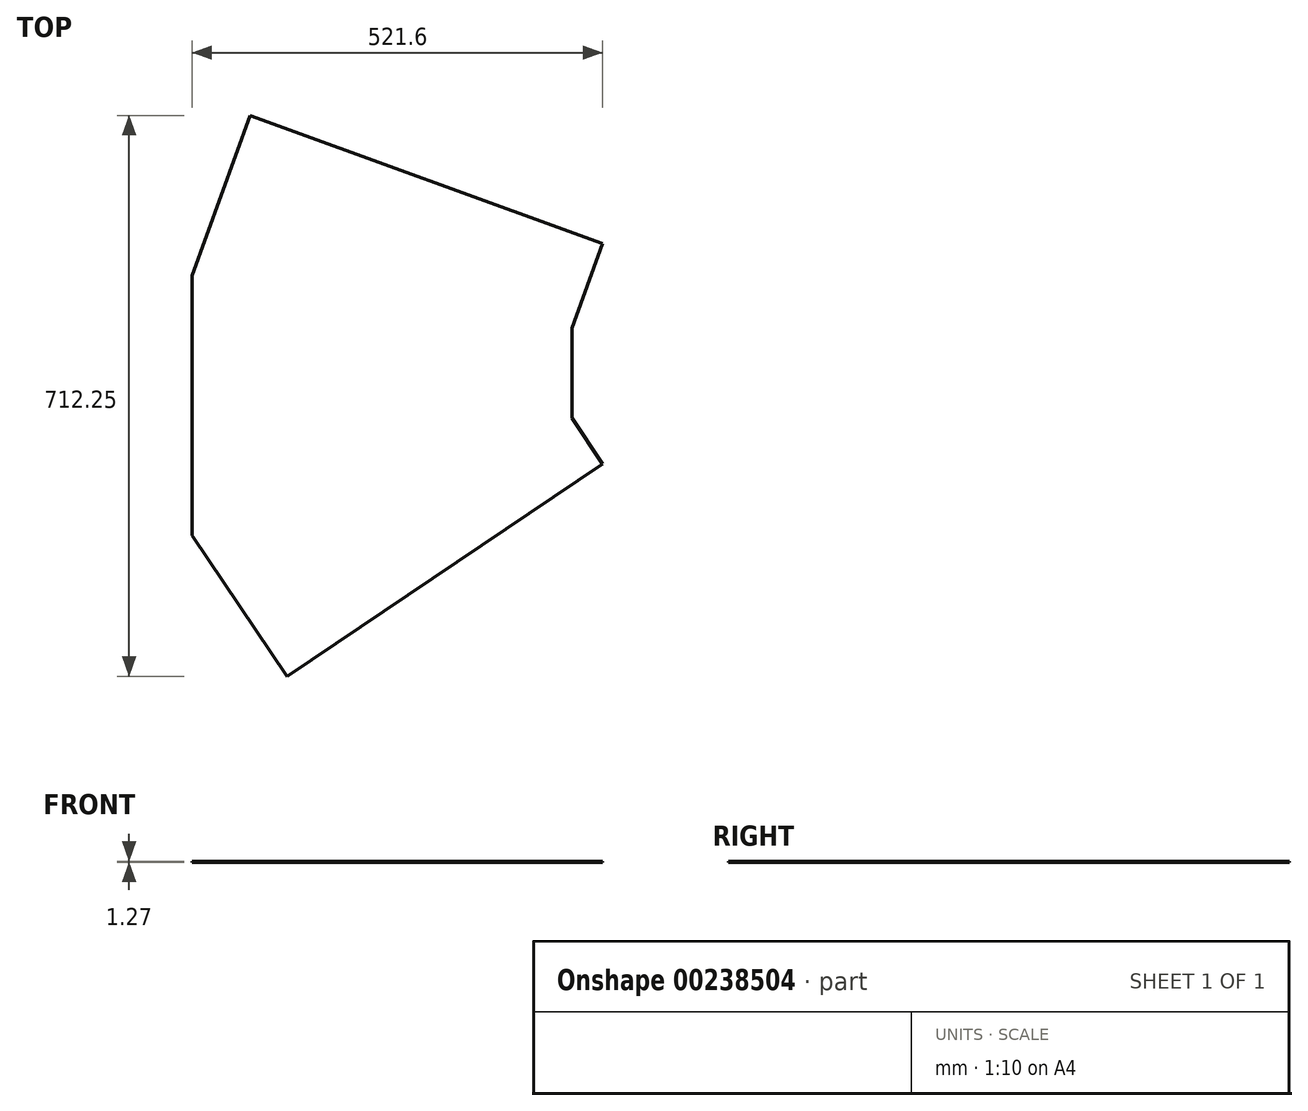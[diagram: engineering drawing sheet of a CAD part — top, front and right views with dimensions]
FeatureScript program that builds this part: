
annotation { "Feature Type Name" : "Feature", "Feature Type Description" : "" }
export const myFeature = defineFeature(function(context is Context, id is Id, definition is map)
    precondition{}
    {
        {
            var Q0;
            Q0=qCreatedBy(makeId("Top.planeOp"),FACE);
            var sketch = newSketch(context, id + "F0", { "sketchPlane" : qUnion([Q0])});
            skLineSegment(sketch, "E0", {"start": v(0, 0) * mm, "end": v(0, -330.2) * mm});
            skLineSegment(sketch, "E1", {"start": v(120.56, -509.3) * mm, "end": v(0, -330.2) * mm});
            skLineSegment(sketch, "E2", {"start": v(521.6, -239.36) * mm, "end": v(120.56, -509.3) * mm});
            skLineSegment(sketch, "E3", {"start": v(482.6, -181.41) * mm, "end": v(521.6, -239.36) * mm});
            skLineSegment(sketch, "E4", {"start": v(482.6, -181.41) * mm, "end": v(482.6, -67.11) * mm});
            skLineSegment(sketch, "E5", {"start": v(482.6, -67.11) * mm, "end": v(521.6, 40.33) * mm});
            skLineSegment(sketch, "E6", {"start": v(521.6, 40.33) * mm, "end": v(73.67, 202.94) * mm});
            skLineSegment(sketch, "E7", {"start": v(73.67, 202.94) * mm, "end": v(0, 0) * mm});
            skSolve(sketch);
        }
        {
            var Q0;
            Q0 = qSketchRegion(id + "F0", true);
            extrude(context, id + "F1", {"entities" : qUnion([Q0]), "depth" : 1.27 * mm});
        }
    });
